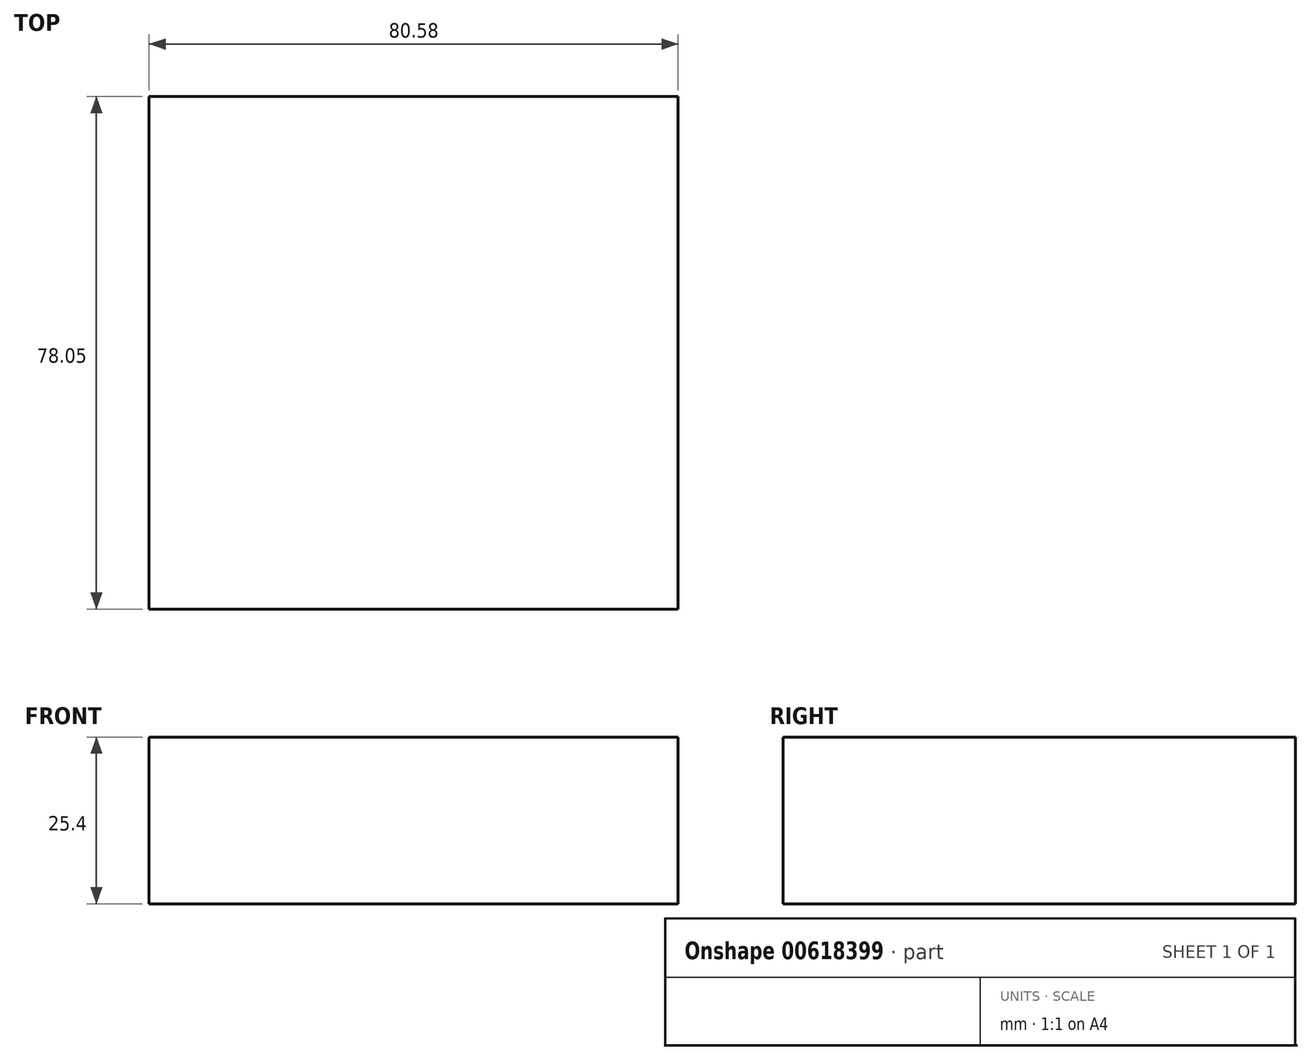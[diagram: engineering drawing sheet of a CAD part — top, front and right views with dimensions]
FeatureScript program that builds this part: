
annotation { "Feature Type Name" : "Feature", "Feature Type Description" : "" }
export const myFeature = defineFeature(function(context is Context, id is Id, definition is map)
    precondition{}
    {
        {
            var Q0;
            Q0=qCreatedBy(makeId("Top.planeOp"),FACE);
            var sketch = newSketch(context, id + "F0", { "sketchPlane" : qUnion([Q0])});
            skLineSegment(sketch, "E0.bottom", {"start": v(40.15, -33.71) * mm, "end": v(-40.43, -33.71) * mm});
            skLineSegment(sketch, "E0.top", {"start": v(40.15, 44.34) * mm, "end": v(-40.43, 44.34) * mm});
            skLineSegment(sketch, "E0.left", {"start": v(40.15, -33.71) * mm, "end": v(40.15, 44.34) * mm});
            skLineSegment(sketch, "E0.right", {"start": v(-40.43, -33.71) * mm, "end": v(-40.43, 44.34) * mm});
            skSolve(sketch);
        }
        {
            var Q0;
            Q0 = qSketchRegion(id + "F0", true);
            extrude(context, id + "F1", {"entities" : qUnion([Q0]), "depth" : 25.4 * mm, "offsetDistance" : 25.4 * mm});
        }
    });
